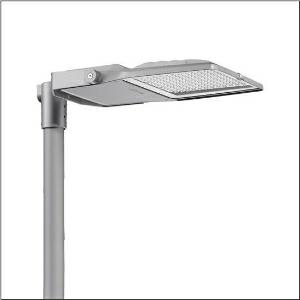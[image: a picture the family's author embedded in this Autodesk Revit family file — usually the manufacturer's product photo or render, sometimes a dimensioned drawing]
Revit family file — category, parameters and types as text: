
# Revit family: floodlight_fl_21_midi___pl64_5xa7786e4e3a_f47e
name_source: partatom
category: Lighting Fixtures
units: mm (PartAtom-declared; Revit-internal decimal feet)

## family parameters
Cut with Voids When Loaded = No
Host = Face
Light Source = No
Part Type = Normal
Room Calculation Point = No
Round Connector Dimension = Use Diameter
Shared = No

## types (1)
- --- (1 x LED, 27140 lm, 212.4 W, 4000K)
    Apparent Load = 212 VA
    CIE Flux Codes = 28 80 98 100 100
    Color Rendering = 70
    Color Temperature = 4000K
    Default Elevation = 1800 mm
    Description = Floodlight FL 21 midi, floodlight, primary light control with lens, of PMMA, primary optical cover: protective disc, of toughened safety glass, transparent, light distribution: PL64, light emission: direct distribution, installation type: surface-mounted, LED, High Power LED, rated luminous flux: 27.140lm, luminous efficacy: 128lm/W, light colour: 740, colour temperature: 4000K, control gear: Smart Interface (Zhaga)D4i, control: overheat protection, constant luminous flux control, time-dependent luminous flux control, flexible luminous flux parameterisation, pre-setting: logarithmic dimming characteristic, with terminal, 6-pole, mains connection: 220..240V, AC, 50/60Hz, start of lifetime: 212W, end of service life: 231W, reduction: 95W, mast bracket, of diecast aluminium, powder-coated, Siteco® metallic grey (DB 702S), corrosivity category C5 mid according to DIN EN ISO 12944, suitable for swimming pools, chlorine-resistant, sealing non-destructively replaceable, mast bracket, of steel, galvanised, powder-coated, Siteco® metallic grey (DB 702S), Smart Interface below and above, protection rating (complete): IP66, insulation class (complete): insulation class II (safety insulation), certification: CE, ENEC, VDE, protection symbol: D, impact resistance: IK08, permissible operating ambient temperature: -40..+40°C, permissible operating ambient temperature for outdoor applications: -40..+50°C, standard: DIN EN 12944, LABS conformity tested according to VDMA 24364:2018-05, packaging unit: 1 piece

Light Distribution: PL64
    Height = 76 mm
    Lamp = 1 x LED
    Lamp Light Flux = 27140 lm
    Lamp Power = 212.4 W
    Lamp count = 1
    Length = 657 mm
    Luminous efficacy = 128 lm/W
    Manufacturer = Siteco
    ModVariant = No
    Model = 5XA7786E4E3A
    Number of Poles = 1
    OnlyDefault = Yes
    Power Factor = 1
    Product Name = Floodlight FL 21 midi | PL64
    Product group = floodlight | pylon annexe
    ProductGroupID = 6200
    Protection Class = Protection class II
    Protection Degree = IP 66
    RLX_Detail_Level = 1
    RLX_Emergency_Light_Flux = 0 lm
    RLX_Emergency_Type = 0
    RLX_Emergency_Type_DB = No
    RlxData = <blob elided: 104581 chars, md5=d3dc38a7>
    Socket = socket
    Standby Power = 0 W
    System Light Flux = 27140 lm
    System Power = 212 W
    Type Comments = factory setting: luminous flux: 100 % | dim-lin: 254 | 710 mA
    Type Image = l_1007123.jpg
    URL = http://relux.com
    VarID = @adj_089412
    Voltage = 0 V
    Weight = 0.00 kg
    Width = 442 mm

## geometry (parser evidence)
native form markers: Blend x4, Sweep x11
no freeform markers — native parametric forms only
